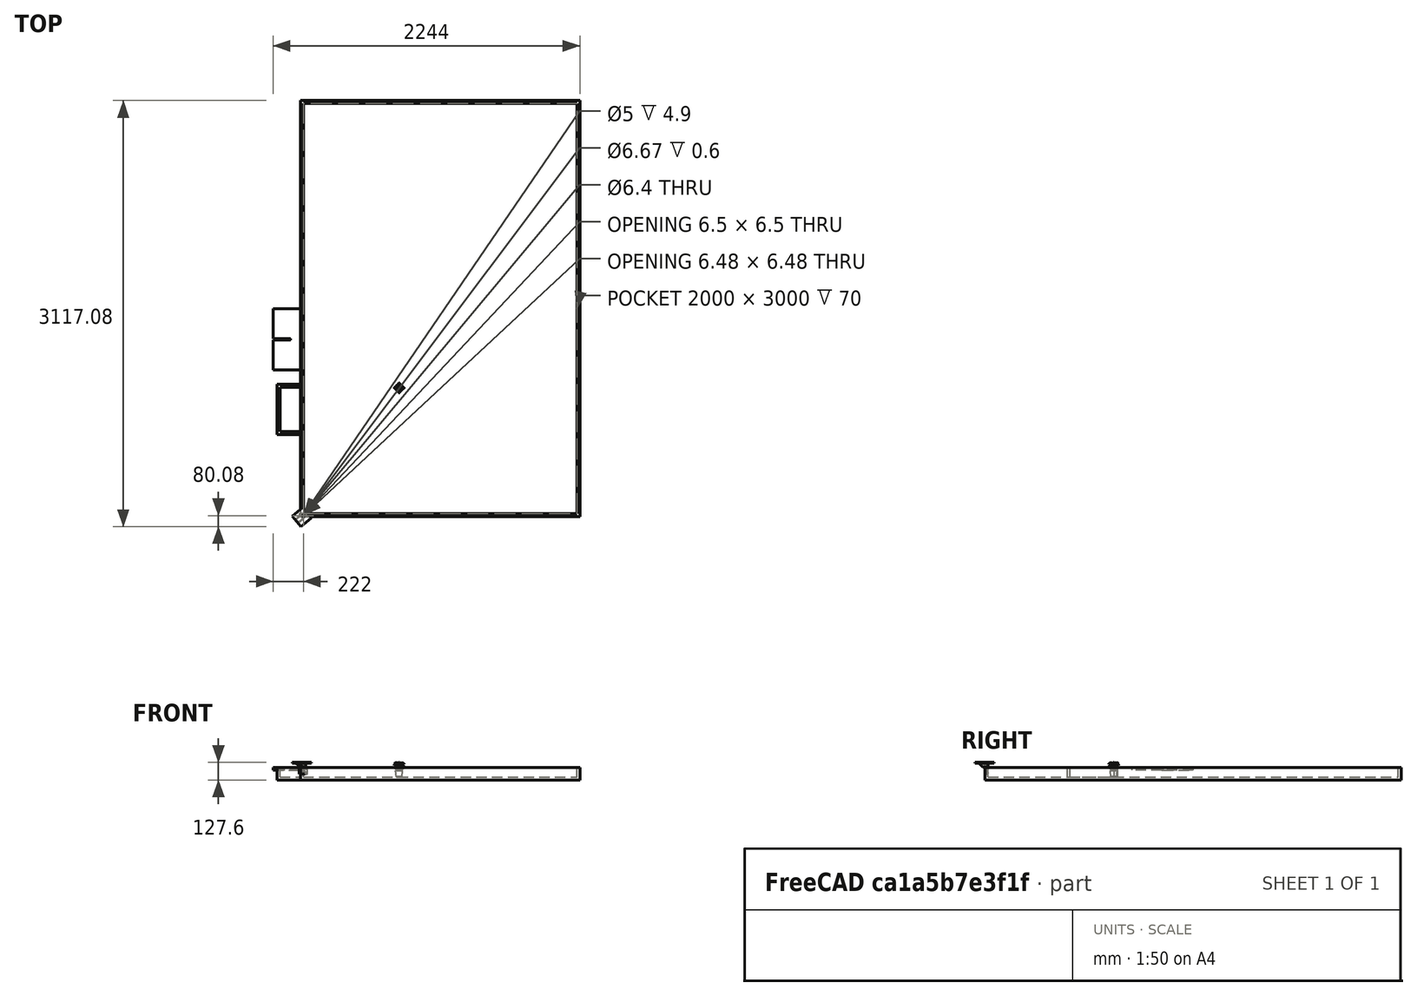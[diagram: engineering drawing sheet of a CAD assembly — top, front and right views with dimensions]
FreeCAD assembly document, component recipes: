
FREECAD ASSEMBLY — COMPONENT RECIPES ("table_2024")

This assembly document has 3 components, labeled P0..P2 below (a component is one placed body or linked part). 1 of them carries a construction recipe — the FreeCAD feature program that regenerates the part from scratch, quoted from this document or its linked companion documents; the rest are supplied as boundary geometry only. No exploded tour is included for this assembly.
COMPONENT P0 — geometry summary ("Link026(*plante)"; no construction recipe available for this part):
  bounding box: 105.5 x 76.1 x 76.1 mm
  tessellated surface: 8,838 triangles
  volume: 86039 mm^3 (14% of its bounding box)
  symmetry: 4-fold rotationally symmetric about the z axis; mirror-symmetric across its x mid-plane, y mid-plane
COMPONENT P1 — geometry summary ("Table 2024"; no construction recipe available for this part):
  bounding box: 3388.0 x 2311.1 x 127.6 mm
  tessellated surface: 661,092 triangles
  volume: 21993719 mm^3 (2% of its bounding box)
COMPONENT P2 — recipe-attached ("Table", modeled in this document).
Construction recipe (the document's own serialized feature program — sketch geometry with constraints, then the solid features built on it; lengths are millimeters unless a unit is written):

FEATURE [Sketcher::SketchObject] Sketch
  ArcFitTolerance = 1e-06
  AttachmentSupport = -> [XY_Plane]
  ExternalBSplineMaxDegree = 5
  ExternalBSplineTolerance = 0.0001
  FullyConstrained = true
  InternalTolerance = 1e-06
  InvalidShape = false
  MakeInternals = true
  MapMode = 5
  Support = -> [XY_Plane]
  TreeRank = 102
  ValidateShape = true
  sketch-geometry (4):
    g0: LineSegment StartX=-6.17e-14 StartY=9.4e-15 StartZ=0 EndX=2000 EndY=9.4e-15 EndZ=0
    g1: LineSegment StartX=2000 StartY=9.4e-15 StartZ=0 EndX=2000 EndY=3000 EndZ=0
    g2: LineSegment StartX=2000 StartY=3000 StartZ=0 EndX=0 EndY=3000 EndZ=0
    g3: LineSegment StartX=-6.17e-14 StartY=3000 StartZ=0 EndX=-6.17e-14 EndY=0 EndZ=0
  constraints (11):
    c: Coincident(g0,g1)
    c: Coincident(g1,g2)
    c: Coincident(g2,g3)
    c: Coincident(g3,g0)
    c: Horizontal(g0)
    c: Horizontal(g2)
    c: Vertical(g1)
    c: Vertical(g3)
    c: Coincident(g0,g-1)
    c: DistanceX(g2,g2) = 2000
    c: DistanceY(g1,g1) = 3000
FEATURE [PartDesign::Pad] Pad
  AddSubType = 0
  AlongSketchNormal = false
  AutoTaperInnerAngle = true
  CheckUpToFaceLimits = true
  ClaimChildren = false
  Direction = (0,0,1)
  Fit = 0
  FitJoin = 0
  InnerFit = 0
  InnerFitJoin = 0
  InvalidShape = false
  Length = 22
  Length2 = 100
  Linearize = true
  NewSolid = false
  Profile = -> Sketch
  Refine = true
  Reversed = true
  Suppress = false
  TaperInnerAngle = 0
  TaperInnerAngleRev = 0
  TreeRank = 103
  Type = 0
  ValidateShape = true
  _ProfileBasedVersion = 1
FEATURE [Sketcher::SketchObject] Sketch001
  ArcFitTolerance = 1e-06
  AttachmentSupport = -> [XY_Plane]
  ExternalBSplineMaxDegree = 5
  ExternalBSplineTolerance = 0.0001
  FullyConstrained = true
  InternalTolerance = 1e-06
  InvalidShape = false
  MakeInternals = true
  MapMode = 5
  Support = -> [XY_Plane]
  TreeRank = 104
  ValidateShape = true
  sketch-geometry (8):
    g0: LineSegment StartX=9.49e-14 StartY=1.886e-13 StartZ=0 EndX=2000 EndY=1.886e-13 EndZ=0
    g1: LineSegment StartX=2000 StartY=1.886e-13 StartZ=0 EndX=2000 EndY=3000 EndZ=0
    g2: LineSegment StartX=2000 StartY=3000 StartZ=0 EndX=0 EndY=3000 EndZ=0
    g3: LineSegment StartX=9.49e-14 StartY=3000 StartZ=0 EndX=9.49e-14 EndY=0 EndZ=0
    g4: LineSegment StartX=-22 StartY=-22 StartZ=0 EndX=2022 EndY=-22 EndZ=0
    g5: LineSegment StartX=2022 StartY=-22 StartZ=0 EndX=2022 EndY=3022 EndZ=0
    g6: LineSegment StartX=2022 StartY=3022 StartZ=0 EndX=-22 EndY=3022 EndZ=0
    g7: LineSegment StartX=-22 StartY=3022 StartZ=0 EndX=-22 EndY=-22 EndZ=0
  constraints (23):
    c: Coincident(g0,g1)
    c: Coincident(g1,g2)
    c: Coincident(g2,g3)
    c: Coincident(g3,g0)
    c: Horizontal(g0)
    c: Horizontal(g2)
    c: Vertical(g1)
    c: Vertical(g3)
    c: Coincident(g0,g-1)
    c: Coincident(g4,g5)
    c: Coincident(g5,g6)
    c: Coincident(g6,g7)
    c: Coincident(g7,g4)
    c: Horizontal(g4)
    c: Horizontal(g6)
    c: Vertical(g5)
    c: Vertical(g7)
    c: DistanceX(g4,g0) = 22
    c: DistanceY(g4,g0) = 22
    c: DistanceX(g2,g2) = 2000
    c: DistanceY(g1,g1) = 3000
    c: DistanceX(g1,g5) = 22
    c: DistanceY(g1,g5) = 22
FEATURE [PartDesign::Pad] Pad001
  AddSubType = 0
  AlongSketchNormal = false
  AutoTaperInnerAngle = true
  BaseFeature = -> Pad
  CheckUpToFaceLimits = true
  ClaimChildren = false
  Direction = (0,0,1)
  Fit = 0
  FitJoin = 0
  InnerFit = 0
  InnerFitJoin = 0
  InvalidShape = false
  Length = 70
  Length2 = 22
  Linearize = true
  NewSolid = false
  Profile = -> Sketch001
  Refine = true
  Suppress = false
  TaperInnerAngle = 0
  TaperInnerAngleRev = 0
  TreeRank = 105
  Type = 4
  ValidateShape = true
  _ProfileBasedVersion = 1
FEATURE [PartDesign::Body] Body  label="BaseTable"
  AutoGroupSolids = false
  ClaimAllChildren = false
  ExportMode = 0
  Group = -> [Sketch,Pad,Sketch001,Pad001]
  InvalidShape = false
  Origin = -> Origin
  SingleSolid = true
  Tip = -> Pad001
  TreeRank = 101
  ValidateShape = true
  _ExportChildren = -> [Pad,Pad001]
  _GroupVersion = 1
FEATURE [Sketcher::SketchObject] Sketch002
  ArcFitTolerance = 1e-06
  AttachmentSupport = -> [XY_Plane011]
  ExternalBSplineMaxDegree = 5
  ExternalBSplineTolerance = 0.0001
  FullyConstrained = true
  InternalTolerance = 1e-06
  InvalidShape = false
  MakeInternals = true
  MapMode = 5
  Support = -> [XY_Plane011]
  TreeRank = 116
  ValidateShape = true
  sketch-geometry (9):
    g0: LineSegment StartX=-7.371e-13 StartY=-22 StartZ=0 EndX=450 EndY=-22 EndZ=0
    g1: LineSegment StartX=450 StartY=-22 StartZ=0 EndX=450 EndY=-222 EndZ=0
    g2: LineSegment [constr] StartX=450 StartY=-222 StartZ=0 EndX=-7.39e-13 EndY=-222 EndZ=0
    g3: LineSegment StartX=-7.371e-13 StartY=-222 StartZ=0 EndX=-7.371e-13 EndY=-22 EndZ=0
    g4: LineSegment StartX=220 StartY=-222 StartZ=0 EndX=220 EndY=-100 EndZ=0
    g5: LineSegment StartX=230 StartY=-222 StartZ=0 EndX=230 EndY=-100 EndZ=0
    g6: ArcOfCircle CenterX=225 CenterY=-100 CenterZ=0 NormalX=0 NormalY=0 NormalZ=1 AngleXU=0 Radius=5 StartAngle=-8.5425e-12 EndAngle=3.14159
    g7: LineSegment StartX=220 StartY=-222 StartZ=0 EndX=-7.39e-13 EndY=-222 EndZ=0
    g8: LineSegment StartX=230 StartY=-222 StartZ=0 EndX=450 EndY=-222 EndZ=0
  constraints (25):
    c: Coincident(g0,g1)
    c: Coincident(g1,g2)
    c: Coincident(g2,g3)
    c: Coincident(g3,g0)
    c: Horizontal(g0)
    c: Horizontal(g2)
    c: Vertical(g1)
    c: Vertical(g3)
    c: PointOnObject(g0,g-2)
    c: DistanceY(g1,g1) = 200
    c: DistanceY(g0,g-1) = 22
    c: DistanceX(g2,g2) = 450
    c: PointOnObject(g4,g2)
    c: Vertical(g4)
    c: PointOnObject(g5,g2)
    c: Vertical(g5)
    c: Tangent(g6,g5) = -1.5708
    c: Tangent(g6,g4) = 1.5708
    c: Coincident(g7,g4)
    c: Coincident(g7,g3)
    c: Coincident(g8,g5)
    c: Coincident(g8,g1)
    c: Equal(g8,g7)
    c: DistanceX(g4,g5) = 10
    c: DistanceY(g1,g6) = 122
FEATURE [PartDesign::Pad] Pad002
  AddSubType = 0
  AlongSketchNormal = false
  AutoTaperInnerAngle = true
  CheckUpToFaceLimits = true
  ClaimChildren = false
  Direction = (0,0,1)
  Fit = 0
  FitJoin = 0
  InnerFit = 0
  InnerFitJoin = 0
  InvalidShape = false
  Length = 22
  Length2 = 100
  Linearize = true
  NewSolid = false
  Profile = -> Sketch002
  Refine = true
  Reversed = true
  Suppress = false
  TaperInnerAngle = 0
  TaperInnerAngleRev = 0
  TreeRank = 117
  Type = 0
  ValidateShape = true
  _ProfileBasedVersion = 1
FEATURE [PartDesign::Body] Body010  label="ZoneCalculBleu"
  AutoGroupSolids = false
  ClaimAllChildren = false
  ExportMode = 0
  Group = -> [Sketch002,Pad002]
  InvalidShape = false
  Origin = -> Origin015
  Placement = pos=(3.331e-13,1500,70) rot=(0,0,-1;1.5708rad)
  SingleSolid = true
  Tip = -> Pad002
  TreeRank = 115
  ValidateShape = true
  _ExportChildren = -> [Pad002]
  _GroupVersion = 1
PROVENANCE & LICENSES
A FreeCAD (.FCStd) document from a public repository crawl; recipes are the document's own serialized feature recipes (and, for linked parts, companion documents' recipes).
License: as declared in the source repository (recorded in the dataset sidecar).
